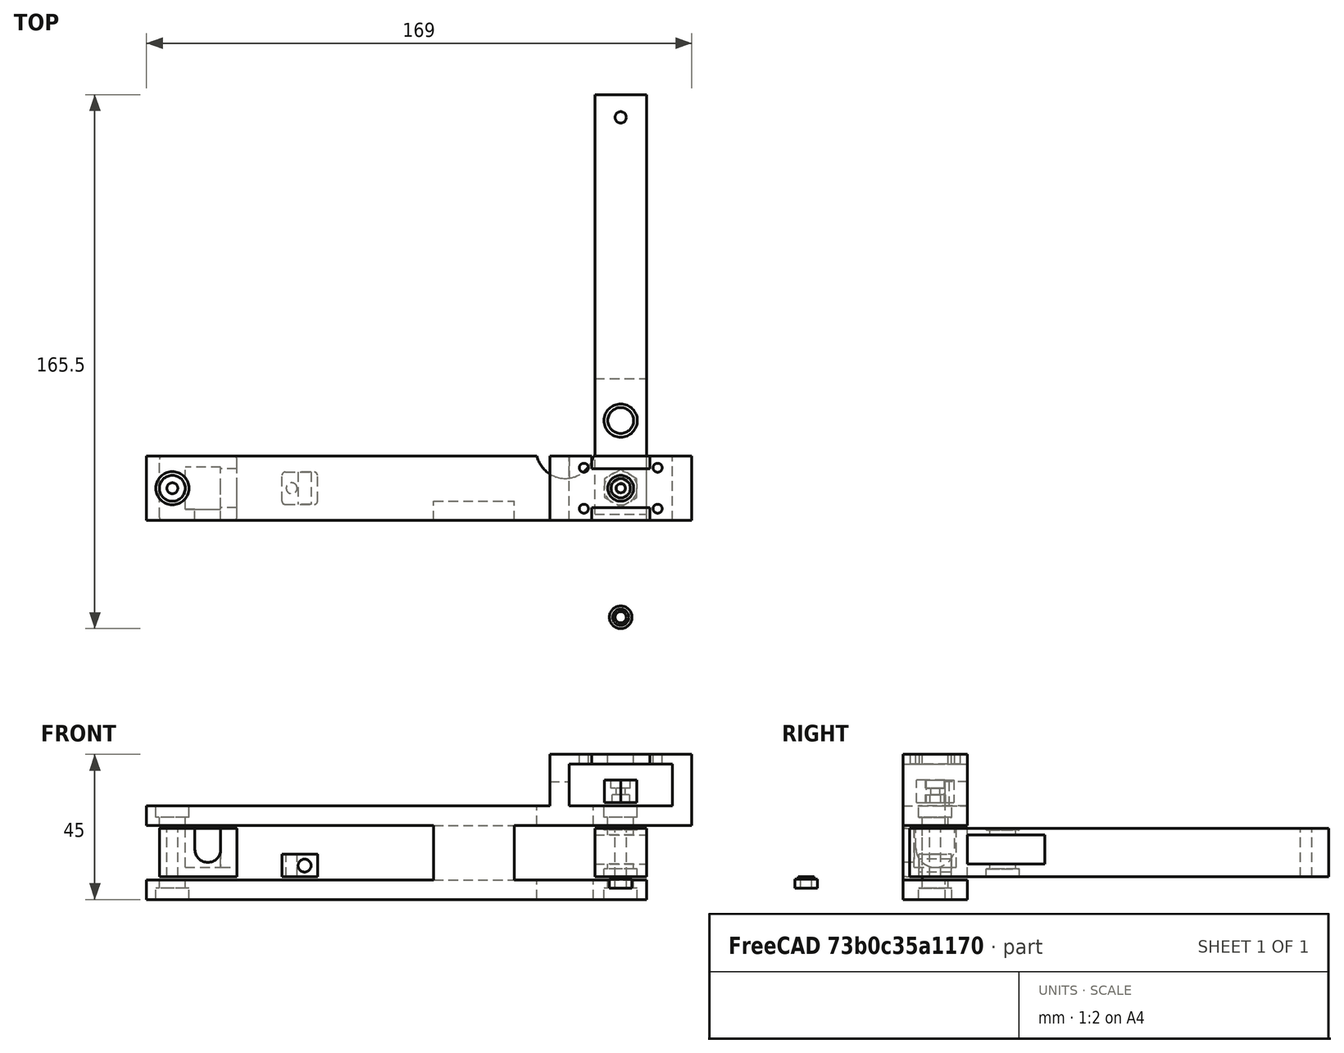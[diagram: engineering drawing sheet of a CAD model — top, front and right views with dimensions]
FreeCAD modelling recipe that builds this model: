
FCSTD DOCUMENT  (FreeCAD 0.15R4671 (Git))
Label: pneumatic
License: All rights reserved
LicenseURL: http://en.wikipedia.org/wiki/All_rights_reserved
objects: Part::Cut×44, Part::Cylinder×29, Part::Box×27, Part::Fillet×8, Part::Fuse×6
note: 114 computed .brp shape members not serialized (recipe doc carries the construction recipe); baked Part::Feature solids carry a one-line shape summary decoded from their .brp

FEATURE [Part::Box] Box  label="Cube"
  Height = 7
  Length = 11
  Placement = pos=(-3,-5,0) rot=(0,0,1;0rad)
  Width = 10
FEATURE [Part::Cylinder] Cylinder
  Angle = 360
  Height = 10
  Placement = pos=(0,0,-1) rot=(0,0,1;0rad)
  Radius = 1.7
FEATURE [Part::Cylinder] Cylinder001
  Angle = 360
  Height = 13
  Placement = pos=(4,6,3.5) rot=(1,0,0;1.5708rad)
  Radius = 2
FEATURE [Part::Cut] Cut
  Base = -> Box
  Tool = -> Cylinder
FEATURE [Part::Cut] Cut001  label="piston-rod-axis"
  Base = -> Cut
  Tool = -> Cylinder001
FEATURE [Part::Box] Box001  label="Cube001"
  Height = 15
  Length = 24
  Placement = pos=(-5,0,0) rot=(0,0,1;0rad)
  Width = 20
FEATURE [Part::Box] Box002  label="Cube002"
  Height = 17
  Length = 11
  Placement = pos=(3,3.5,3) rot=(0,0,1;0rad)
  Width = 13
FEATURE [Part::Cut] Cut002
  Base = -> Box001
  Tool = -> Box002
FEATURE [Part::Cylinder] Cylinder002
  Angle = 360
  Height = 10
  Placement = pos=(12,10,9) rot=(0,1,0;1.5708rad)
  Radius = 6
FEATURE [Part::Box] Box003  label="Cube003"
  Height = 10
  Length = 10
  Placement = pos=(12,4,9) rot=(0,0,1;0rad)
  Width = 12
FEATURE [Part::Cut] Cut003
  Base = -> Cut002
  Tool = -> Cylinder002
FEATURE [Part::Cylinder] Cylinder003
  Angle = 360
  Height = 23
  Placement = pos=(-1,10,-1) rot=(0,0,1;0rad)
  Radius = 1.7
FEATURE [Part::Cylinder] Cylinder005
  Angle = 360
  Height = 17
  Placement = pos=(10,8,8.5) rot=(1,0,0;1.5708rad)
  Radius = 4
FEATURE [Part::Box] Box004  label="Cube004"
  Height = 10
  Length = 8
  Placement = pos=(6,-3,8.5) rot=(0,0,1;0rad)
  Width = 10
FEATURE [Part::Cylinder] Cylinder006
  Angle = 360
  Height = 4
  Placement = pos=(-37,0,18.5) rot=(0,0,1;0rad)
  Radius = 5.15
FEATURE [Part::Box] Box005  label="Cube005"
  Height = 6
  Length = 155
  Placement = pos=(-45,-10,-7) rot=(0,0,1;0rad)
  Width = 20
FEATURE [Part::Cylinder] Cylinder007
  Angle = 360
  Height = 4
  Placement = pos=(-37,0,-7.5) rot=(0,0,1;0rad)
  Radius = 5.15
FEATURE [Part::Box] Box006  label="Cube006"
  Height = 6
  Length = 169
  Placement = pos=(-45,-10,16) rot=(0,0,1;0rad)
  Width = 20
FEATURE [Part::Box] Box007  label="Cube007"
  Height = 15
  Length = 16
  Placement = pos=(94,-8,0) rot=(0,0,1;0rad)
  Width = 130
FEATURE [Part::Cylinder] Cylinder008
  Angle = 360
  Height = 4
  Placement = pos=(102,0,-7.5) rot=(0,0,1;0rad)
  Radius = 5.15
FEATURE [Part::Cylinder] Cylinder009
  Angle = 360
  Height = 4
  Placement = pos=(102,0,18.5) rot=(0,0,1;0rad)
  Radius = 5.15
FEATURE [Part::Cylinder] Cylinder010
  Angle = 360
  Height = 7
  Placement = pos=(102,0,23) rot=(0,0,1;0rad)
  Radius = 6
FEATURE [Part::Cylinder] Cylinder011
  Angle = 360
  Height = 3
  Placement = pos=(102,0,27.5) rot=(0,0,1;0rad)
  Radius = 3
FEATURE [Part::Cylinder] Cylinder012
  Angle = 360
  Height = 19
  Placement = pos=(102,0,18.5) rot=(0,0,1;0rad)
  Radius = 1.4
FEATURE [Part::Cylinder] Cylinder013
  Angle = 360
  Height = 3
  Placement = pos=(102,0,22.5) rot=(0,0,1;0rad)
  Radius = 4
FEATURE [Part::Box] Box008  label="Cube008"
  Height = 10
  Length = 10
  Placement = pos=(89.33,-5,17) rot=(0,0,1;0rad)
  Width = 10
FEATURE [Part::Box] Box009  label="Cube009"
  Height = 10
  Length = 10
  Placement = pos=(99.9951,-13.4725,17) rot=(0,0,1;1.0472rad)
  Width = 10
FEATURE [Part::Box] Box010  label="Cube010"
  Height = 10
  Length = 10
  Placement = pos=(112.665,-8.47254,17) rot=(0,0,1;2.0944rad)
  Width = 10
FEATURE [Part::Box] Box011  label="Cube011"
  Height = 10
  Length = 10
  Placement = pos=(114.67,5,17) rot=(0,0,1;3.14159rad)
  Width = 10
FEATURE [Part::Box] Box012  label="Cube012"
  Height = 10
  Length = 10
  Placement = pos=(104.005,13.4725,17) rot=(0,0,1;4.18879rad)
  Width = 10
FEATURE [Part::Box] Box013  label="Cube013"
  Height = 10
  Length = 10
  Placement = pos=(91.3349,8.47254,17) rot=(0,0,-1;1.0472rad)
  Width = 10
FEATURE [Part::Cut] Cut010
  Base = -> Cylinder013
  Tool = -> Box008
FEATURE [Part::Cut] Cut011
  Base = -> Cut010
  Tool = -> Box013
FEATURE [Part::Cut] Cut012
  Base = -> Cut011
  Tool = -> Box012
FEATURE [Part::Cut] Cut013
  Base = -> Cut012
  Tool = -> Box011
FEATURE [Part::Cut] Cut014
  Base = -> Cut013
  Tool = -> Box010
FEATURE [Part::Cut] Cut015
  Base = -> Cut014
  Tool = -> Box009
FEATURE [Part::Cylinder] Cylinder014
  Angle = 360
  Height = 27
  Placement = pos=(113.43,6.35,27.5) rot=(0,0,1;0rad)
  Radius = 1.4
FEATURE [Part::Cylinder] Cylinder015
  Angle = 360
  Height = 28
  Placement = pos=(113.43,-6.35,25.5) rot=(0,0,1;0rad)
  Radius = 1.4
FEATURE [Part::Cylinder] Cylinder016
  Angle = 360
  Height = 27
  Placement = pos=(90.57,6.35,25.5) rot=(0,0,1;0rad)
  Radius = 1.4
FEATURE [Part::Cylinder] Cylinder017
  Angle = 360
  Height = 29
  Placement = pos=(90.57,-6.35,25.5) rot=(0,0,1;0rad)
  Radius = 1.4
FEATURE [Part::Box] Box014  label="Cube014"
  Height = 3
  Length = 44
  Placement = pos=(80,-10,35) rot=(0,0,1;0rad)
  Width = 20
FEATURE [Part::Box] Box015  label="Cube015"
  Height = 13
  Length = 6
  Placement = pos=(80,-10,22) rot=(0,0,1;0rad)
  Width = 20
FEATURE [Part::Box] Box016  label="Cube016"
  Height = 5
  Length = 18
  Placement = pos=(93,-11,34) rot=(0,0,1;0rad)
  Width = 5
FEATURE [Part::Box] Box017  label="Cube017"
  Height = 5
  Length = 18
  Placement = pos=(93,6,34) rot=(0,0,1;0rad)
  Width = 5
FEATURE [Part::Box] Box018  label="Cube018"
  Height = 13
  Length = 6
  Placement = pos=(118,-10,22) rot=(0,0,1;0rad)
  Width = 20
FEATURE [Part::Fuse] Fusion001
  Base = -> Box006
  Tool = -> Box015
FEATURE [Part::Fuse] Fusion002
  Base = -> Box018
  Tool = -> Fusion001
FEATURE [Part::Fuse] Fusion003
  Base = -> Box014
  Tool = -> Fusion002
FEATURE [Part::Cut] Cut017
  Base = -> Fusion003
  Tool = -> Box017
FEATURE [Part::Cut] Cut018
  Base = -> Cut017
  Tool = -> Box016
FEATURE [Part::Cut] Cut019
  Base = -> Cut018
  Tool = -> Cylinder017
FEATURE [Part::Cut] Cut020
  Base = -> Cut019
  Tool = -> Cylinder016
FEATURE [Part::Cut] Cut021
  Base = -> Cut020
  Tool = -> Cylinder015
FEATURE [Part::Cut] Cut022
  Base = -> Cut021
  Tool = -> Cylinder014
FEATURE [Part::Cylinder] Cylinder018
  Angle = 360
  Height = 8
  Placement = pos=(102,0,32) rot=(0,0,1;0rad)
  Radius = 4
FEATURE [Part::Cut] Cut023  label="top-arm"
  Base = -> Cut022
  Tool = -> Cylinder018
FEATURE [Part::Cut] Cut024
  Base = -> Cut003
  Tool = -> Box003
FEATURE [Part::Cut] Cut025
  Base = -> Cut024
  Tool = -> Cylinder005
FEATURE [Part::Cut] Cut026
  Base = -> Cut025
  Tool = -> Box004
FEATURE [Part::Cut] Cut027
  Base = -> Cut026
  Placement = pos=(1,-10,0) rot=(0,0,1;0rad)
  Tool = -> Cylinder003
FEATURE [Part::Fillet] Fillet004
  Base = -> Cut027
  Edges = 1 edges r=1: [Edge1]
FEATURE [Part::Fillet] Fillet005
  Base = -> Fillet004
  Edges = 1 edges r=1: [Edge3]
FEATURE [Part::Fillet] Fillet006
  Base = -> Fillet005
  Edges = 1 edges r=1: [Edge25]
FEATURE [Part::Fillet] Fillet007  label="cylinder-holder"
  Base = -> Fillet006
  Edges = 1 edges r=1: [Edge25]
  Placement = pos=(-37,0,0) rot=(0,0,1;0rad)
FEATURE [Part::Cylinder] Cylinder019
  Angle = 360
  Height = 31
  Placement = pos=(-37,0,-7.5) rot=(0,0,1;0rad)
  Radius = 4
FEATURE [Part::Cylinder] Cylinder020
  Angle = 360
  Height = 31
  Placement = pos=(102,0,-7.5) rot=(0,0,1;0rad)
  Radius = 4
FEATURE [Part::Cylinder] Cylinder021
  Angle = 360
  Height = 20
  Placement = pos=(102,0,-7.5) rot=(0,0,1;0rad)
  Radius = 1.75
FEATURE [Part::Cylinder] Cylinder022
  Angle = 360
  Height = 2.75
  Placement = pos=(102,0,-3.5) rot=(0,0,1;0rad)
  Radius = 3.5
FEATURE [Part::Box] Box019  label="Cube019"
  Height = 17
  Length = 25
  Placement = pos=(44,-10,-1) rot=(0,0,1;0rad)
  Width = 6
FEATURE [Part::Fuse] Fusion
  Base = -> Box005
  Tool = -> Box019
FEATURE [Part::Fuse] Fusion004
  Base = -> Cut023
  Tool = -> Fusion
FEATURE [Part::Cut] Cut029
  Base = -> Fusion004
  Tool = -> Cylinder006
FEATURE [Part::Cut] Cut030
  Base = -> Cut029
  Tool = -> Cylinder008
FEATURE [Part::Cut] Cut031
  Base = -> Cut030
  Tool = -> Cylinder009
FEATURE [Part::Cut] Cut032
  Base = -> Cut031
  Tool = -> Cylinder007
FEATURE [Part::Cut] Cut033
  Base = -> Cut032
  Tool = -> Cylinder019
FEATURE [Part::Cut] Cut034  label="main-arm1"
  Base = -> Cut033
  Tool = -> Cylinder020
FEATURE [Part::Cylinder] Cylinder023
  Angle = 360
  Height = 3.5
  Placement = pos=(102,0,-3.5) rot=(0,0,1;0rad)
  Radius = 2.5
FEATURE [Part::Fuse] Fusion005
  Base = -> Cylinder022
  Tool = -> Cylinder023
FEATURE [Part::Cut] Cut035  label="spacer"
  Base = -> Fusion005
  Placement = pos=(0,-40,0) rot=(0,0,1;0rad)
  Tool = -> Cylinder021
FEATURE [Part::Box] Box020  label="Cube020"
  Height = 10
  Length = 10
  Placement = pos=(107,-5,22) rot=(0,0,1;0rad)
  Width = 10
FEATURE [Part::Box] Box021  label="Cube021"
  Height = 10
  Length = 10
  Placement = pos=(108.83,1.83013,22) rot=(0,0,1;1.0472rad)
  Width = 10
FEATURE [Part::Box] Box022  label="Cube022"
  Height = 10
  Length = 10
  Placement = pos=(103.83,6.83013,22) rot=(0,0,1;2.0944rad)
  Width = 10
FEATURE [Part::Box] Box023  label="Cube023"
  Height = 10
  Length = 10
  Placement = pos=(97,5,22) rot=(0,0,1;3.14159rad)
  Width = 10
FEATURE [Part::Box] Box024  label="Cube024"
  Height = 10
  Length = 10
  Placement = pos=(100.17,-6.83013,22) rot=(0,0,-1;1.0472rad)
  Width = 10
FEATURE [Part::Box] Box025  label="Cube025"
  Height = 10
  Length = 10
  Placement = pos=(95.1699,-1.83013,22) rot=(0,0,-1;2.0944rad)
  Width = 10
FEATURE [Part::Cut] Cut036
  Base = -> Cylinder010
  Tool = -> Box020
FEATURE [Part::Cut] Cut037
  Base = -> Cut036
  Tool = -> Box025
FEATURE [Part::Cut] Cut038
  Base = -> Cut037
  Tool = -> Box024
FEATURE [Part::Cut] Cut039
  Base = -> Cut038
  Tool = -> Box023
FEATURE [Part::Cut] Cut040
  Base = -> Cut039
  Tool = -> Box022
FEATURE [Part::Cut] Cut041
  Base = -> Cut040
  Tool = -> Box021
FEATURE [Part::Cut] Cut042
  Base = -> Cut041
  Tool = -> Cylinder011
FEATURE [Part::Cut] Cut043
  Base = -> Cut042
  Tool = -> Cylinder012
FEATURE [Part::Cut] Cut044  label="magnet-holder"
  Base = -> Cut043
  Tool = -> Cut015
FEATURE [Part::Cylinder] Cylinder024
  Angle = 360
  Height = 4
  Placement = pos=(102,21,-1.5) rot=(0,0,1;0rad)
  Radius = 5.15
FEATURE [Part::Cylinder] Cylinder025
  Angle = 360
  Height = 4
  Placement = pos=(102,21,14.5) rot=(0,0,1;0rad)
  Radius = 5.15
FEATURE [Part::Cylinder] Cylinder026
  Angle = 360
  Height = 31
  Placement = pos=(102,21,-7.5) rot=(0,0,1;0rad)
  Radius = 4
FEATURE [Part::Cylinder] Cylinder027
  Angle = 360
  Height = 31
  Placement = pos=(102,0,-7.5) rot=(0,0,1;0rad)
  Radius = 1.75
FEATURE [Part::Box] Box026  label="Cube026"
  Height = 9
  Length = 27
  Placement = pos=(91,10,4) rot=(0,0,1;0rad)
  Width = 24
FEATURE [Part::Cylinder] Cylinder028
  Angle = 360
  Height = 47
  Placement = pos=(84.7978,12.0451,-17.5) rot=(0,0,1;0.959931rad)
  Radius = 9
FEATURE [Part::Cut] Cut045  label="main-arm"
  Base = -> Cut034
  Tool = -> Cylinder028
FEATURE [Part::Cut] Cut046
  Base = -> Box007
  Tool = -> Cylinder024
FEATURE [Part::Cut] Cut047
  Base = -> Cut046
  Tool = -> Box026
FEATURE [Part::Cut] Cut048
  Base = -> Cut047
  Tool = -> Cylinder027
FEATURE [Part::Cut] Cut049
  Base = -> Cut048
  Tool = -> Cylinder026
FEATURE [Part::Cut] Cut050  label="moved-arm1"
  Base = -> Cut049
  Tool = -> Cylinder025
FEATURE [Part::Cylinder] Cylinder029
  Angle = 360
  Height = 31
  Placement = pos=(102,115,-7.5) rot=(0,0,1;0rad)
  Radius = 1.75
FEATURE [Part::Cut] Cut051  label="moved-arm"
  Base = -> Cut050
  Tool = -> Cylinder029
FEATURE [Part::Fillet] Fillet
  Base = -> Cut001
  Edges = 1 edges r=1: [Edge13]
FEATURE [Part::Fillet] Fillet008
  Base = -> Fillet
  Edges = 1 edges r=1: [Edge15]
FEATURE [Part::Fillet] Fillet009
  Base = -> Fillet008
  Edges = 1 edges r=1: [Edge19]
FEATURE [Part::Fillet] Fillet010  label="piston-pivot"
  Base = -> Fillet009
  Edges = 1 edges r=1: [Edge17]
